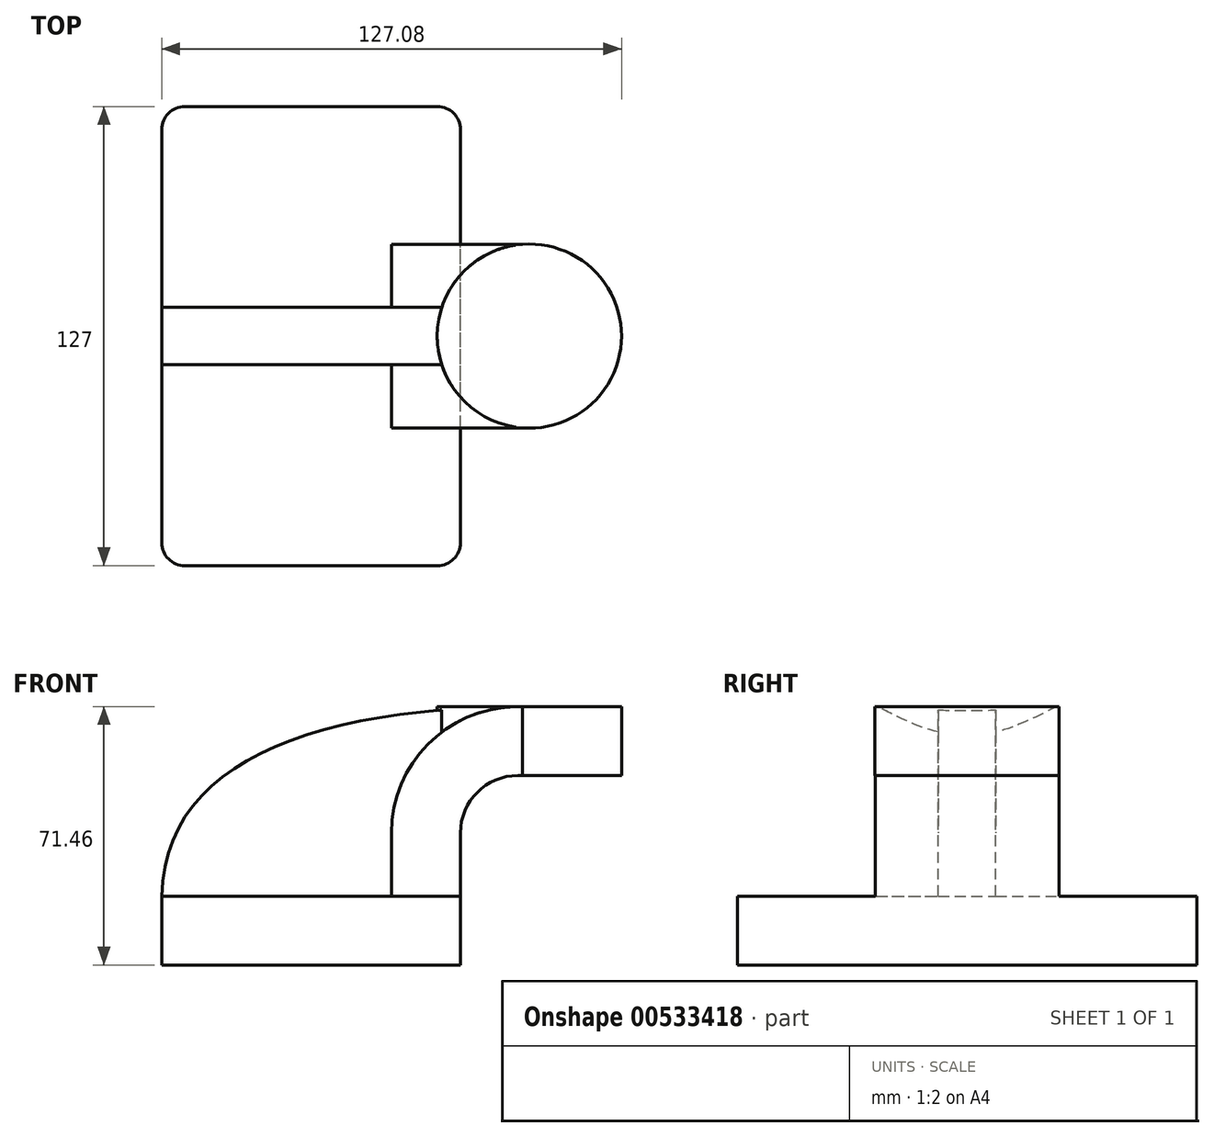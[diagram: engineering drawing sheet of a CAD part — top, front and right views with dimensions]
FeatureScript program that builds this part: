
annotation { "Feature Type Name" : "Feature", "Feature Type Description" : "" }
export const myFeature = defineFeature(function(context is Context, id is Id, definition is map)
    precondition{}
    {
        {
            var Q0;
            Q0=qCreatedBy(makeId("Front.planeOp"),FACE);
            var sketch = newSketch(context, id + "F0", { "sketchPlane" : qUnion([Q0])});
            skLineSegment(sketch, "E0.bottom", {"start": v(-41.28, 9.52) * mm, "end": v(41.27, 9.53) * mm});
            skLineSegment(sketch, "E0.top", {"start": v(-41.28, -9.53) * mm, "end": v(41.28, -9.53) * mm});
            skLineSegment(sketch, "E0.left", {"start": v(-41.28, 9.52) * mm, "end": v(-41.28, -9.53) * mm});
            skLineSegment(sketch, "E0.right", {"start": v(41.27, 9.53) * mm, "end": v(41.28, -9.52) * mm});
            skPoint(sketch, "E0.middle", {"position": v(0, 0) * mm});
            skLineSegment(sketch, "E1", {"start": v(41.27, 9.53) * mm, "end": v(41.27, 27) * mm});
            skLineSegment(sketch, "E2.bottom", {"start": v(111.12, 38.1) * mm, "end": v(60.32, 38.1) * mm});
            skLineSegment(sketch, "E2.top", {"start": v(111.12, 66.67) * mm, "end": v(60.32, 66.67) * mm});
            skLineSegment(sketch, "E2.left", {"start": v(111.12, 38.1) * mm, "end": v(111.12, 66.68) * mm});
            skLineSegment(sketch, "E2.right", {"start": v(60.32, 38.1) * mm, "end": v(60.32, 66.68) * mm});
            skPoint(sketch, "E2.middle", {"position": v(85.72, 52.39) * mm});
            skArc(sketch, "E3", {"start": v(41.27, 27) * mm, "mid": v(45.93, 38.22) * mm, "end": v(57.16, 42.88) * mm});
            skLineSegment(sketch, "E4", {"start": v(57.16, 42.88) * mm, "end": v(85.8, 42.88) * mm});
            skLineSegment(sketch, "E5.0", {"start": v(57.16, 61.93) * mm, "end": v(85.8, 61.93) * mm});
            skArc(sketch, "E5.1", {"start": v(22.22, 27) * mm, "mid": v(32.46, 51.7) * mm, "end": v(57.16, 61.93) * mm});
            skLineSegment(sketch, "E5.2", {"start": v(22.22, 9.53) * mm, "end": v(22.22, 27) * mm});
            skLineSegment(sketch, "E6", {"start": v(85.8, 61.93) * mm, "end": v(85.8, 42.88) * mm});
            skFitSpline(sketch, "E7", {"points": [v(-41.28, 9.52) * mm, v(57.16, 61.93) * mm], "startDerivative": vector(2.12, 110.55) * mm, "endDerivative": vector(171.47, 1.52) * mm});
            skSolve(sketch);
        }
        {
            var Q0;
            Q0=makeQuery(id+"F0.imprint","IMPRINT",FACE,{"disambiguationData":[TD([[makeQuery(id+"F0.imprint","IMPRINT",EDGE,{"derivedFrom":sQuery(id+"F0.wireOp",EDGE,"E0.top")}),1.0]])]});
            extrude(context, id + "F1", {"entities" : qUnion([Q0]), "endBound" : BoundingType.SYMMETRIC, "depth" : 127 * mm, "offsetDistance" : 25.4 * mm});
        }
        {
            var Q0;
            {var subQ1=sQuery(id+"F0.wireOp",EDGE,"E1");Q0=makeQuery(id+"F0.imprint","IMPRINT",FACE,{"disambiguationData":[TD([[makeQuery(id+"F0.imprint","IMPRINT",EDGE,{"derivedFrom":subQ1}),1.0]])]});}
            extrude(context, id + "F2", {"entities" : qUnion([Q0]), "operationType" : NewBodyOperationType.ADD, "endBound" : BoundingType.SYMMETRIC, "depth" : 50.8 * mm, "offsetDistance" : 25.4 * mm});
        }
        {
            var Q0;
            {var subQ3=sQuery(id+"F0.wireOp",EDGE,"E5.2");Q0=makeQuery(id+"F0.imprint","IMPRINT",FACE,{"disambiguationData":[TD([[makeQuery(id+"F0.imprint","IMPRINT",EDGE,{"derivedFrom":subQ3}),1.0]])]});}
            extrude(context, id + "F3", {"entities" : qUnion([Q0]), "operationType" : NewBodyOperationType.ADD, "endBound" : BoundingType.SYMMETRIC, "depth" : 15.88 * mm, "offsetDistance" : 25.4 * mm});
        }
        {
            var Q0;
            {var subQ5=sQuery(id+"F0.wireOp",EDGE,"E6");Q0=makeQuery(id+"F0.imprint","IMPRINT",FACE,{"disambiguationData":[TD([[makeQuery(id+"F0.imprint","IMPRINT",EDGE,{"derivedFrom":subQ5}),-1.0]])]});}
            var Q1;
            Q1=sQuery(id+"F0.wireOp",EDGE,"E2.right");
            revolve(context, id + "F4", {"operationType" : NewBodyOperationType.ADD, "entities" : qUnion([Q0]), "axis" : qUnion([Q1]), "revolveType" : RevolveType.FULL});
        }
        {
            var Q0;
            Q0=makeQuery(id+"F1.opExtrude","CAP_EDGE",EDGE,{"disambiguationData":[OSD([sQuery(id+"F0.wireOp",EDGE,"E0.right")])],"isStart":true});
            var Q1;
            Q1=makeQuery(id+"F1.opExtrude","CAP_EDGE",EDGE,{"disambiguationData":[OSD([sQuery(id+"F0.wireOp",EDGE,"E0.left")])],"isStart":true});
            var Q2;
            Q2=makeQuery(id+"F1.opExtrude","CAP_EDGE",EDGE,{"disambiguationData":[OSD([sQuery(id+"F0.wireOp",EDGE,"E0.right")])],"isStart":false});
            var Q3;
            Q3=makeQuery(id+"F1.opExtrude","CAP_EDGE",EDGE,{"disambiguationData":[OSD([sQuery(id+"F0.wireOp",EDGE,"E0.left")])],"isStart":false});
            fillet(context, id + "F5", {"entities" : qUnion([Q0, Q1, Q2, Q3]), "radius" : 6.35 * mm, "tangentPropagation" : true, "allowEdgeOverflow" : false});
        }
    });
